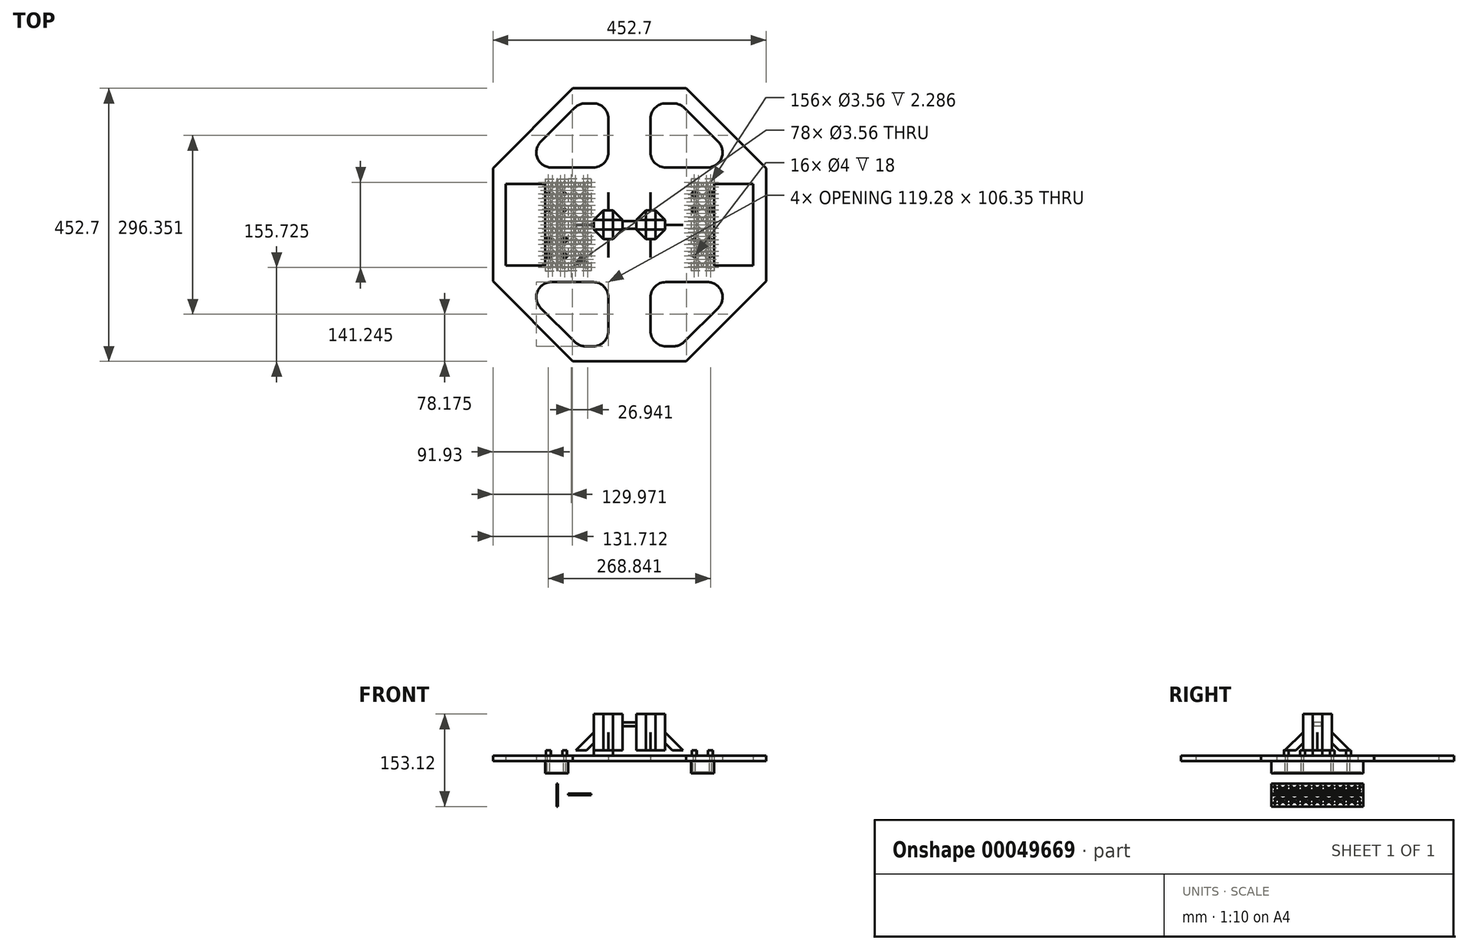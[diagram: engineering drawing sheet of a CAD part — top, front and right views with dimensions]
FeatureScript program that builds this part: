
annotation { "Feature Type Name" : "Feature", "Feature Type Description" : "" }
export const myFeature = defineFeature(function(context is Context, id is Id, definition is map)
    precondition{}
    {
        {
            var Q0;
            Q0=qCreatedBy(makeId("Top.planeOp"),FACE);
            var sketch = newSketch(context, id + "F0", { "sketchPlane" : qUnion([Q0])});
            skCircle(sketch, "E0.cCircle", {"center": v(0, 0) * mm, "radius": 245 * mm, "construction": true});
            skLineSegment(sketch, "E0.0", {"start": v(93.76, -226.35) * mm, "end": v(-93.76, -226.35) * mm});
            skLineSegment(sketch, "E0.1", {"start": v(-93.76, -226.35) * mm, "end": v(-226.35, -93.76) * mm});
            skLineSegment(sketch, "E0.2", {"start": v(-226.35, -93.76) * mm, "end": v(-226.35, 93.76) * mm});
            skLineSegment(sketch, "E0.3", {"start": v(-226.35, 93.76) * mm, "end": v(-93.76, 226.35) * mm});
            skLineSegment(sketch, "E0.4", {"start": v(-93.76, 226.35) * mm, "end": v(93.76, 226.35) * mm});
            skLineSegment(sketch, "E0.5", {"start": v(93.76, 226.35) * mm, "end": v(226.35, 93.76) * mm});
            skLineSegment(sketch, "E0.6", {"start": v(226.35, 93.76) * mm, "end": v(226.35, -93.76) * mm});
            skLineSegment(sketch, "E0.7", {"start": v(226.35, -93.76) * mm, "end": v(93.76, -226.35) * mm});
            skLineSegment(sketch, "E1", {"start": v(0, 226.35) * mm, "end": v(0, -226.35) * mm, "construction": true});
            skLineSegment(sketch, "E2.bottom", {"start": v(-205, 67.5) * mm, "end": v(-140, 67.5) * mm});
            skLineSegment(sketch, "E2.top", {"start": v(-205, -67.5) * mm, "end": v(-140, -67.5) * mm});
            skLineSegment(sketch, "E2.left", {"start": v(-205, 67.5) * mm, "end": v(-205, -67.5) * mm});
            skLineSegment(sketch, "E2.right", {"start": v(-140, 67.5) * mm, "end": v(-140, -67.5) * mm});
            skLineSegment(sketch, "E3.MirrorCS", {"start": v(205, 67.5) * mm, "end": v(205, -67.5) * mm});
            skLineSegment(sketch, "E4.MirrorCS", {"start": v(205, 67.5) * mm, "end": v(140, 67.5) * mm});
            skLineSegment(sketch, "E5.MirrorCS", {"start": v(205, -67.5) * mm, "end": v(140, -67.5) * mm});
            skLineSegment(sketch, "E6.MirrorCS", {"start": v(140, 67.5) * mm, "end": v(140, -67.5) * mm});
            skLineSegment(sketch, "E7.0", {"start": v(-90.72, -194.03) * mm, "end": v(-147.07, -137.68) * mm});
            skLineSegment(sketch, "E8.0", {"start": v(-226.35, -95) * mm, "end": v(-225.1, -95) * mm});
            skLineSegment(sketch, "E9.trimOffspring", {"start": v(-129.4, -95) * mm, "end": v(-60, -95) * mm});
            skLineSegment(sketch, "E10.trimOffspring", {"start": v(-60, -201.35) * mm, "end": v(-73.05, -201.35) * mm});
            skLineSegment(sketch, "E11.trimOffspring", {"start": v(-35, -120) * mm, "end": v(-35, -176.35) * mm});
            skPoint(sketch, "E12.visualSharp", {"position": v(-189.75, -95) * mm});
            skArc(sketch, "E12.filletArc", {"start": v(-129.4, -95) * mm, "mid": v(-152.5, -110.43) * mm, "end": v(-147.07, -137.68) * mm});
            skPoint(sketch, "E13.visualSharp", {"position": v(-35, -95) * mm});
            skArc(sketch, "E13.filletArc", {"start": v(-35, -120) * mm, "mid": v(-42.32, -102.32) * mm, "end": v(-60, -95) * mm});
            skPoint(sketch, "E14.visualSharp", {"position": v(-35, -201.35) * mm});
            skArc(sketch, "E14.filletArc", {"start": v(-60, -201.35) * mm, "mid": v(-42.32, -194.03) * mm, "end": v(-35, -176.35) * mm});
            skPoint(sketch, "E15.visualSharp", {"position": v(-83.4, -201.35) * mm});
            skArc(sketch, "E15.filletArc", {"start": v(-90.72, -194.03) * mm, "mid": v(-82.61, -199.45) * mm, "end": v(-73.05, -201.35) * mm});
            skArc(sketch, "E16.MirrorCS", {"start": v(90.72, -194.03) * mm, "mid": v(82.61, -199.45) * mm, "end": v(73.05, -201.35) * mm});
            skLineSegment(sketch, "E17.MirrorCS", {"start": v(60, -201.35) * mm, "end": v(73.05, -201.35) * mm});
            skArc(sketch, "E18.MirrorCS", {"start": v(35, -120) * mm, "mid": v(42.32, -102.32) * mm, "end": v(60, -95) * mm});
            skArc(sketch, "E19.MirrorCS", {"start": v(60, -201.35) * mm, "mid": v(42.32, -194.03) * mm, "end": v(35, -176.35) * mm});
            skPoint(sketch, "E20.MirrorP", {"position": v(83.4, -201.35) * mm});
            skPoint(sketch, "E21.MirrorP", {"position": v(35, -95) * mm});
            skPoint(sketch, "E22.MirrorP", {"position": v(35, -201.35) * mm});
            skLineSegment(sketch, "E23.MirrorCS", {"start": v(90.72, -194.03) * mm, "end": v(147.07, -137.68) * mm});
            skLineSegment(sketch, "E24.MirrorCS", {"start": v(129.4, -95) * mm, "end": v(60, -95) * mm});
            skLineSegment(sketch, "E25.MirrorCS", {"start": v(35, -120) * mm, "end": v(35, -176.35) * mm});
            skArc(sketch, "E26.MirrorCS", {"start": v(129.4, -95) * mm, "mid": v(152.5, -110.43) * mm, "end": v(147.07, -137.68) * mm});
            skLineSegment(sketch, "E27.MirrorCS", {"start": v(-60, 201.35) * mm, "end": v(-73.05, 201.35) * mm});
            skLineSegment(sketch, "E28.MirrorCS", {"start": v(60, 201.35) * mm, "end": v(73.05, 201.35) * mm});
            skArc(sketch, "E29.MirrorCS", {"start": v(90.72, 194.03) * mm, "mid": v(82.61, 199.45) * mm, "end": v(73.05, 201.35) * mm});
            skArc(sketch, "E30.MirrorCS", {"start": v(-90.72, 194.03) * mm, "mid": v(-82.61, 199.45) * mm, "end": v(-73.05, 201.35) * mm});
            skArc(sketch, "E31.MirrorCS", {"start": v(-35, 120) * mm, "mid": v(-42.32, 102.32) * mm, "end": v(-60, 95) * mm});
            skPoint(sketch, "E32.MirrorP", {"position": v(35, 95) * mm});
            skLineSegment(sketch, "E33.MirrorCS", {"start": v(-35, 120) * mm, "end": v(-35, 176.35) * mm});
            skPoint(sketch, "E34.MirrorP", {"position": v(-35, 95) * mm});
            skPoint(sketch, "E35.MirrorP", {"position": v(-83.4, 201.35) * mm});
            skArc(sketch, "E36.MirrorCS", {"start": v(129.4, 95) * mm, "mid": v(152.5, 110.43) * mm, "end": v(147.07, 137.68) * mm});
            skLineSegment(sketch, "E37.MirrorCS", {"start": v(35, 120) * mm, "end": v(35, 176.35) * mm});
            skPoint(sketch, "E38.MirrorP", {"position": v(83.4, 201.35) * mm});
            skArc(sketch, "E39.MirrorCS", {"start": v(35, 120) * mm, "mid": v(42.32, 102.32) * mm, "end": v(60, 95) * mm});
            skLineSegment(sketch, "E40.MirrorCS", {"start": v(-129.4, 95) * mm, "end": v(-60, 95) * mm});
            skPoint(sketch, "E41.MirrorP", {"position": v(-35, 201.35) * mm});
            skArc(sketch, "E42.MirrorCS", {"start": v(60, 201.35) * mm, "mid": v(42.32, 194.03) * mm, "end": v(35, 176.35) * mm});
            skPoint(sketch, "E43.MirrorP", {"position": v(35, 201.35) * mm});
            skLineSegment(sketch, "E44.MirrorCS", {"start": v(-90.72, 194.03) * mm, "end": v(-147.07, 137.68) * mm});
            skArc(sketch, "E45.MirrorCS", {"start": v(-60, 201.35) * mm, "mid": v(-42.32, 194.03) * mm, "end": v(-35, 176.35) * mm});
            skArc(sketch, "E46.MirrorCS", {"start": v(-129.4, 95) * mm, "mid": v(-152.5, 110.43) * mm, "end": v(-147.07, 137.68) * mm});
            skLineSegment(sketch, "E47.MirrorCS", {"start": v(129.4, 95) * mm, "end": v(60, 95) * mm});
            skLineSegment(sketch, "E48.MirrorCS", {"start": v(90.72, 194.03) * mm, "end": v(147.07, 137.68) * mm});
            skLineSegment(sketch, "E49.bottom", {"start": v(-140, 76.2) * mm, "end": v(-101.9, 76.2) * mm});
            skLineSegment(sketch, "E49.top", {"start": v(-140, -76.2) * mm, "end": v(-101.9, -76.2) * mm});
            skLineSegment(sketch, "E49.left", {"start": v(-140, 76.2) * mm, "end": v(-140, -76.2) * mm});
            skLineSegment(sketch, "E49.right", {"start": v(-101.9, 76.2) * mm, "end": v(-101.9, -76.2) * mm});
            skLineSegment(sketch, "E50.MirrorCS", {"start": v(101.9, 76.2) * mm, "end": v(101.9, -76.2) * mm});
            skLineSegment(sketch, "E51.MirrorCS", {"start": v(140, 76.2) * mm, "end": v(101.9, 76.2) * mm});
            skLineSegment(sketch, "E52.MirrorCS", {"start": v(140, 76.2) * mm, "end": v(140, -76.2) * mm});
            skLineSegment(sketch, "E53.MirrorCS", {"start": v(140, -76.2) * mm, "end": v(101.9, -76.2) * mm});
            skCircle(sketch, "E54", {"center": v(-134.41, 51.56) * mm, "radius": 2 * mm});
            skCircle(sketch, "E55.0.1.0", {"center": v(-134.41, 24.61) * mm, "radius": 2 * mm});
            skCircle(sketch, "E55.1.0.0", {"center": v(-107.46, 51.56) * mm, "radius": 2 * mm});
            skCircle(sketch, "E55.1.1.0", {"center": v(-107.46, 24.61) * mm, "radius": 2 * mm});
            skLineSegment(sketch, "E55.direction1", {"start": v(-134.41, 51.56) * mm, "end": v(-107.46, 51.56) * mm, "construction": true});
            skLineSegment(sketch, "E55.direction2", {"start": v(-134.41, 51.56) * mm, "end": v(-134.41, 24.61) * mm, "construction": true});
            skLineSegment(sketch, "E56", {"start": v(-140, 0) * mm, "end": v(-101.9, 0) * mm, "construction": true});
            skCircle(sketch, "E57.MirrorC", {"center": v(-107.46, -24.61) * mm, "radius": 2 * mm});
            skCircle(sketch, "E58.MirrorC", {"center": v(-134.41, -24.61) * mm, "radius": 2 * mm});
            skCircle(sketch, "E59.MirrorC", {"center": v(-107.46, -51.56) * mm, "radius": 2 * mm});
            skCircle(sketch, "E60.MirrorC", {"center": v(-134.41, -51.56) * mm, "radius": 2 * mm});
            skCircle(sketch, "E61.MirrorC", {"center": v(134.41, 51.56) * mm, "radius": 2 * mm});
            skCircle(sketch, "E62.MirrorC", {"center": v(107.46, 51.56) * mm, "radius": 2 * mm});
            skCircle(sketch, "E63.MirrorC", {"center": v(107.46, 24.61) * mm, "radius": 2 * mm});
            skCircle(sketch, "E64.MirrorC", {"center": v(134.41, 24.61) * mm, "radius": 2 * mm});
            skCircle(sketch, "E65.MirrorC", {"center": v(107.46, -24.61) * mm, "radius": 2 * mm});
            skCircle(sketch, "E66.MirrorC", {"center": v(107.46, -51.56) * mm, "radius": 2 * mm});
            skCircle(sketch, "E67.MirrorC", {"center": v(134.41, -51.56) * mm, "radius": 2 * mm});
            skCircle(sketch, "E68.MirrorC", {"center": v(134.41, -24.61) * mm, "radius": 2 * mm});
            skSolve(sketch);
        }
        {
            var Q0;
            Q0 = qSketchRegion(id + "F0", true);
            var Q1;
            {var subQ3=sQuery(id+"F0.wireOp",EDGE,"E49.bottom");Q1=makeQuery(id+"F0.imprint","IMPRINT",FACE,{"disambiguationData":[TD([[makeQuery(id+"F0.imprint","IMPRINT",EDGE,{"derivedFrom":subQ3}),-1.0]])]});}
            var Q2;
            Q2=makeQuery(id+"F0.imprint","IMPRINT",FACE,{"disambiguationData":[TD([[makeQuery(id+"F0.imprint","IMPRINT",EDGE,{"derivedFrom":sQuery(id+"F0.wireOp",EDGE,"E50.MirrorCS")}),1.0]])]});
            extrude(context, id + "F1", {"entities" : qUnion([Q0, Q1, Q2]), "depth" : 18 * mm});
        }
        {
            var Q0;
            Q0=makeQuery(id+"F1.opExtrude","CAP_FACE",FACE,{"disambiguationData":[OSD([sQuery(id+"F0.wireOp",EDGE,"E0.0"),sQuery(id+"F0.wireOp",EDGE,"E0.1"),sQuery(id+"F0.wireOp",EDGE,"E0.2"),sQuery(id+"F0.wireOp",EDGE,"E0.3"),sQuery(id+"F0.wireOp",EDGE,"E0.4"),sQuery(id+"F0.wireOp",EDGE,"E0.5"),sQuery(id+"F0.wireOp",EDGE,"E0.6"),sQuery(id+"F0.wireOp",EDGE,"E0.7"),sQuery(id+"F0.wireOp",EDGE,"E2.bottom"),sQuery(id+"F0.wireOp",EDGE,"E2.top"),sQuery(id+"F0.wireOp",EDGE,"E2.left"),sQuery(id+"F0.wireOp",EDGE,"E3.MirrorCS"),sQuery(id+"F0.wireOp",EDGE,"E4.MirrorCS"),sQuery(id+"F0.wireOp",EDGE,"E5.MirrorCS"),sQuery(id+"F0.wireOp",EDGE,"E7.0"),sQuery(id+"F0.wireOp",EDGE,"E9.trimOffspring"),sQuery(id+"F0.wireOp",EDGE,"E10.trimOffspring"),sQuery(id+"F0.wireOp",EDGE,"E11.trimOffspring"),sQuery(id+"F0.wireOp",EDGE,"E12.filletArc"),sQuery(id+"F0.wireOp",EDGE,"E13.filletArc"),sQuery(id+"F0.wireOp",EDGE,"E14.filletArc"),sQuery(id+"F0.wireOp",EDGE,"E15.filletArc"),sQuery(id+"F0.wireOp",EDGE,"E16.MirrorCS"),sQuery(id+"F0.wireOp",EDGE,"E17.MirrorCS"),sQuery(id+"F0.wireOp",EDGE,"E18.MirrorCS"),sQuery(id+"F0.wireOp",EDGE,"E19.MirrorCS"),sQuery(id+"F0.wireOp",EDGE,"E23.MirrorCS"),sQuery(id+"F0.wireOp",EDGE,"E24.MirrorCS"),sQuery(id+"F0.wireOp",EDGE,"E25.MirrorCS"),sQuery(id+"F0.wireOp",EDGE,"E26.MirrorCS"),sQuery(id+"F0.wireOp",EDGE,"E27.MirrorCS"),sQuery(id+"F0.wireOp",EDGE,"E28.MirrorCS"),sQuery(id+"F0.wireOp",EDGE,"E29.MirrorCS"),sQuery(id+"F0.wireOp",EDGE,"E30.MirrorCS"),sQuery(id+"F0.wireOp",EDGE,"E31.MirrorCS"),sQuery(id+"F0.wireOp",EDGE,"E33.MirrorCS"),sQuery(id+"F0.wireOp",EDGE,"E36.MirrorCS"),sQuery(id+"F0.wireOp",EDGE,"E37.MirrorCS"),sQuery(id+"F0.wireOp",EDGE,"E39.MirrorCS"),sQuery(id+"F0.wireOp",EDGE,"E40.MirrorCS"),sQuery(id+"F0.wireOp",EDGE,"E42.MirrorCS"),sQuery(id+"F0.wireOp",EDGE,"E44.MirrorCS"),sQuery(id+"F0.wireOp",EDGE,"E45.MirrorCS"),sQuery(id+"F0.wireOp",EDGE,"E46.MirrorCS"),sQuery(id+"F0.wireOp",EDGE,"E47.MirrorCS"),sQuery(id+"F0.wireOp",EDGE,"E48.MirrorCS"),sQuery(id+"F0.wireOp",EDGE,"E49.left"),sQuery(id+"F0.wireOp",EDGE,"E52.MirrorCS")])],"isStart":false});
            var sketch = newSketch(context, id + "F2", { "sketchPlane" : qUnion([Q0])});
            skPoint(sketch, "E69", {"position": v(0, 0) * mm});
            skPoint(sketch, "E70", {"position": v(-35, 0) * mm});
            skLineSegment(sketch, "E71.rect.bottom", {"start": v(-27.06, -7.94) * mm, "end": v(-42.94, -7.94) * mm});
            skLineSegment(sketch, "E71.rect.top", {"start": v(-27.06, 7.94) * mm, "end": v(-42.94, 7.94) * mm});
            skLineSegment(sketch, "E71.rect.left", {"start": v(-27.06, -7.94) * mm, "end": v(-27.06, 7.94) * mm});
            skLineSegment(sketch, "E71.rect.right", {"start": v(-42.94, -7.94) * mm, "end": v(-42.94, 7.94) * mm});
            skLineSegment(sketch, "E72.bottom", {"start": v(-42.94, 7.94) * mm, "end": v(-58.81, 7.94) * mm});
            skLineSegment(sketch, "E72.top", {"start": v(-42.94, -7.94) * mm, "end": v(-58.81, -7.94) * mm});
            skLineSegment(sketch, "E72.left", {"start": v(-42.94, 7.94) * mm, "end": v(-42.94, -7.94) * mm});
            skLineSegment(sketch, "E72.right", {"start": v(-58.81, 7.94) * mm, "end": v(-58.81, -7.94) * mm});
            skLineSegment(sketch, "E73", {"start": v(0, 0) * mm, "end": v(-35, 0) * mm, "construction": true});
            skLineSegment(sketch, "E74", {"start": v(-35, 0) * mm, "end": v(-58.81, 0) * mm, "construction": true});
            skCircle(sketch, "E75", {"center": v(-134.41, 51.56) * mm, "radius": 4 * mm});
            skCircle(sketch, "E76.0.1.0", {"center": v(-134.41, 24.61) * mm, "radius": 4 * mm});
            skCircle(sketch, "E76.1.0.0", {"center": v(-107.46, 51.56) * mm, "radius": 4 * mm});
            skCircle(sketch, "E76.1.1.0", {"center": v(-107.46, 24.61) * mm, "radius": 4 * mm});
            skLineSegment(sketch, "E76.direction1", {"start": v(-134.41, 51.56) * mm, "end": v(-107.46, 51.56) * mm, "construction": true});
            skLineSegment(sketch, "E76.direction2", {"start": v(-134.41, 51.56) * mm, "end": v(-134.41, 24.61) * mm, "construction": true});
            skLineSegment(sketch, "E77", {"start": v(0, 0) * mm, "end": v(0, 46.73) * mm, "construction": true});
            skCircle(sketch, "E78.MirrorC", {"center": v(-107.46, -51.56) * mm, "radius": 4 * mm});
            skCircle(sketch, "E79.MirrorC", {"center": v(-134.41, -51.56) * mm, "radius": 4 * mm});
            skCircle(sketch, "E80.MirrorC", {"center": v(-134.41, -24.61) * mm, "radius": 4 * mm});
            skCircle(sketch, "E81.MirrorC", {"center": v(-107.46, -24.61) * mm, "radius": 4 * mm});
            skCircle(sketch, "E82.MirrorC", {"center": v(107.46, -24.61) * mm, "radius": 4 * mm});
            skCircle(sketch, "E83.MirrorC", {"center": v(107.46, -51.56) * mm, "radius": 4 * mm});
            skCircle(sketch, "E84.MirrorC", {"center": v(134.41, -51.56) * mm, "radius": 4 * mm});
            skCircle(sketch, "E85.MirrorC", {"center": v(134.41, -24.61) * mm, "radius": 4 * mm});
            skCircle(sketch, "E86.MirrorC", {"center": v(107.46, 24.61) * mm, "radius": 4 * mm});
            skCircle(sketch, "E87.MirrorC", {"center": v(134.41, 24.61) * mm, "radius": 4 * mm});
            skCircle(sketch, "E88.MirrorC", {"center": v(134.41, 51.56) * mm, "radius": 4 * mm});
            skCircle(sketch, "E89.MirrorC", {"center": v(107.46, 51.56) * mm, "radius": 4 * mm});
            skSolve(sketch);
        }
        {
            var Q0;
            Q0=makeQuery(id+"F2.imprint","IMPRINT",FACE,{"disambiguationData":[TD([[makeQuery(id+"F2.imprint","IMPRINT",EDGE,{"derivedFrom":sQuery(id+"F2.wireOp",EDGE,"E75")}),1.0]])]});
            var Q1;
            Q1=makeQuery(id+"F2.imprint","IMPRINT",FACE,{"disambiguationData":[TD([[makeQuery(id+"F2.imprint","IMPRINT",EDGE,{"derivedFrom":sQuery(id+"F2.wireOp",EDGE,"E76.1.0.0")}),1.0]])]});
            var Q2;
            Q2=makeQuery(id+"F2.imprint","IMPRINT",FACE,{"disambiguationData":[TD([[makeQuery(id+"F2.imprint","IMPRINT",EDGE,{"derivedFrom":sQuery(id+"F2.wireOp",EDGE,"E76.0.1.0")}),1.0]])]});
            var Q3;
            Q3=makeQuery(id+"F2.imprint","IMPRINT",FACE,{"disambiguationData":[TD([[makeQuery(id+"F2.imprint","IMPRINT",EDGE,{"derivedFrom":sQuery(id+"F2.wireOp",EDGE,"E76.1.1.0")}),1.0]])]});
            var Q4;
            Q4=makeQuery(id+"F2.imprint","IMPRINT",FACE,{"disambiguationData":[TD([[makeQuery(id+"F2.imprint","IMPRINT",EDGE,{"derivedFrom":sQuery(id+"F2.wireOp",EDGE,"E80.MirrorC")}),-1.0]])]});
            var Q5;
            Q5=makeQuery(id+"F2.imprint","IMPRINT",FACE,{"disambiguationData":[TD([[makeQuery(id+"F2.imprint","IMPRINT",EDGE,{"derivedFrom":sQuery(id+"F2.wireOp",EDGE,"E81.MirrorC")}),-1.0]])]});
            var Q6;
            Q6=makeQuery(id+"F2.imprint","IMPRINT",FACE,{"disambiguationData":[TD([[makeQuery(id+"F2.imprint","IMPRINT",EDGE,{"derivedFrom":sQuery(id+"F2.wireOp",EDGE,"E79.MirrorC")}),-1.0]])]});
            var Q7;
            Q7=makeQuery(id+"F2.imprint","IMPRINT",FACE,{"disambiguationData":[TD([[makeQuery(id+"F2.imprint","IMPRINT",EDGE,{"derivedFrom":sQuery(id+"F2.wireOp",EDGE,"E78.MirrorC")}),-1.0]])]});
            var Q8;
            Q8=makeQuery(id+"F2.imprint","IMPRINT",FACE,{"disambiguationData":[TD([[makeQuery(id+"F2.imprint","IMPRINT",EDGE,{"derivedFrom":sQuery(id+"F2.wireOp",EDGE,"E89.MirrorC")}),-1.0]])]});
            var Q9;
            Q9=makeQuery(id+"F2.imprint","IMPRINT",FACE,{"disambiguationData":[TD([[makeQuery(id+"F2.imprint","IMPRINT",EDGE,{"derivedFrom":sQuery(id+"F2.wireOp",EDGE,"E88.MirrorC")}),-1.0]])]});
            var Q10;
            Q10=makeQuery(id+"F2.imprint","IMPRINT",FACE,{"disambiguationData":[TD([[makeQuery(id+"F2.imprint","IMPRINT",EDGE,{"derivedFrom":sQuery(id+"F2.wireOp",EDGE,"E86.MirrorC")}),-1.0]])]});
            var Q11;
            Q11=makeQuery(id+"F2.imprint","IMPRINT",FACE,{"disambiguationData":[TD([[makeQuery(id+"F2.imprint","IMPRINT",EDGE,{"derivedFrom":sQuery(id+"F2.wireOp",EDGE,"E87.MirrorC")}),-1.0]])]});
            var Q12;
            Q12=makeQuery(id+"F2.imprint","IMPRINT",FACE,{"disambiguationData":[TD([[makeQuery(id+"F2.imprint","IMPRINT",EDGE,{"derivedFrom":sQuery(id+"F2.wireOp",EDGE,"E82.MirrorC")}),1.0]])]});
            var Q13;
            Q13=makeQuery(id+"F2.imprint","IMPRINT",FACE,{"disambiguationData":[TD([[makeQuery(id+"F2.imprint","IMPRINT",EDGE,{"derivedFrom":sQuery(id+"F2.wireOp",EDGE,"E85.MirrorC")}),1.0]])]});
            var Q14;
            Q14=makeQuery(id+"F2.imprint","IMPRINT",FACE,{"disambiguationData":[TD([[makeQuery(id+"F2.imprint","IMPRINT",EDGE,{"derivedFrom":sQuery(id+"F2.wireOp",EDGE,"E83.MirrorC")}),1.0]])]});
            var Q15;
            Q15=makeQuery(id+"F2.imprint","IMPRINT",FACE,{"disambiguationData":[TD([[makeQuery(id+"F2.imprint","IMPRINT",EDGE,{"derivedFrom":sQuery(id+"F2.wireOp",EDGE,"E84.MirrorC")}),1.0]])]});
            var Q16;
            Q16=sQuery(id+"F2.wireOp",EDGE,"E75");
            extrude(context, id + "F3", {"entities" : qUnion([Q0, Q1, Q2, Q3, Q4, Q5, Q6, Q7, Q8, Q9, Q10, Q11, Q12, Q13, Q14, Q15]), "operationType" : NewBodyOperationType.REMOVE, "surfaceEntities" : qUnion([Q16]), "oppositeDirection" : true, "depth" : 9 * mm});
        }
        {
            var Q0;
            Q0=makeQuery(id+"F2.imprint","IMPRINT",FACE,{"disambiguationData":[TD([[makeQuery(id+"F2.imprint","IMPRINT",EDGE,{"derivedFrom":sQuery(id+"F2.wireOp",EDGE,"E72.bottom")}),1.0]])]});
            extrude(context, id + "F4", {"entities" : qUnion([Q0]), "depth" : 60 * mm});
        }
        {
            var Q0;
            Q0=makeQuery(id+"F4.opExtrude","CAP_FACE",FACE,{"disambiguationData":[OSD([sQuery(id+"F2.wireOp",EDGE,"E72.bottom"),sQuery(id+"F2.wireOp",EDGE,"E72.top"),sQuery(id+"F2.wireOp",EDGE,"E72.left"),sQuery(id+"F2.wireOp",EDGE,"E72.right")])],"isStart":false});
            var sketch = newSketch(context, id + "F5", { "sketchPlane" : qUnion([Q0])});
            skLineSegment(sketch, "E90", {"start": v(-42.94, -7.94) * mm, "end": v(-42.94, -23.81) * mm});
            skLineSegment(sketch, "E91", {"start": v(-42.94, -23.81) * mm, "end": v(-58.81, -7.94) * mm});
            skLineSegment(sketch, "E92", {"start": v(-58.81, 0) * mm, "end": v(-42.94, 0) * mm, "construction": true});
            skSolve(sketch);
        }
        {
            var Q0;
            Q0=makeQuery(id+"F5.imprint","IMPRINT",FACE,{"disambiguationData":[TD([[makeQuery(id+"F5.imprint","IMPRINT",EDGE,{"derivedFrom":sQuery(id+"F5.wireOp",EDGE,"E90")}),-1.0]])]});
            extrude(context, id + "F6", {"entities" : qUnion([Q0]), "oppositeDirection" : true, "depth" : 1 / 101.6 * mm});
        }
        {
            var Q0;
            Q0=qCreatedBy(makeId("Front.planeOp"),FACE);
            var sketch = newSketch(context, id + "F7", { "sketchPlane" : qUnion([Q0])});
            skLineSegment(sketch, "E93", {"start": v(0, 0) * mm, "end": v(-35, 0) * mm, "construction": true});
            skLineSegment(sketch, "E94", {"start": v(-35, 0) * mm, "end": v(-35, 90.39) * mm, "construction": true});
            skLineSegment(sketch, "E95.0.0", {"start": v(-58.81, 18) * mm, "end": v(-42.94, 18) * mm, "construction": true});
            skLineSegment(sketch, "E95.0.1", {"start": v(-42.94, 18) * mm, "end": v(-42.94, 78) * mm, "construction": true});
            skLineSegment(sketch, "E95.0.2", {"start": v(-42.94, 78) * mm, "end": v(-58.81, 78) * mm, "construction": true});
            skLineSegment(sketch, "E95.0.3", {"start": v(-58.81, 78) * mm, "end": v(-58.81, 18) * mm, "construction": true});
            skLineSegment(sketch, "E96", {"start": v(-58.81, 30.04) * mm, "end": v(-58.81, 48) * mm});
            skLineSegment(sketch, "E97", {"start": v(-70.85, 18) * mm, "end": v(-88.81, 18) * mm});
            skLineSegment(sketch, "E98", {"start": v(-88.81, 18) * mm, "end": v(-58.81, 48) * mm});
            skLineSegment(sketch, "E99.0", {"start": v(-70.85, 18) * mm, "end": v(-58.81, 30.04) * mm});
            skSolve(sketch);
        }
        {
            var Q0;
            Q0=makeQuery(id+"F7.imprint","IMPRINT",FACE,{"disambiguationData":[TD([[makeQuery(id+"F7.imprint","IMPRINT",EDGE,{"derivedFrom":sQuery(id+"F7.wireOp",EDGE,"E96")}),1.0]])]});
            extrude(context, id + "F8", {"entities" : qUnion([Q0]), "depth" : 1 / 203.2 * mm, "hasSecondDirection" : true, "secondDirectionOppositeDirection" : true, "secondDirectionDepth" : 1 / 203.2 * mm});
        }
        {
            var Q0;
            Q0=makeQuery(id+"F4.opExtrude","SWEPT_BODY",BODY,{"disambiguationData":[OSD([sQuery(id+"F2.wireOp",EDGE,"E72.bottom"),sQuery(id+"F2.wireOp",EDGE,"E72.top"),sQuery(id+"F2.wireOp",EDGE,"E72.left"),sQuery(id+"F2.wireOp",EDGE,"E72.right")])]});
            var Q1;
            Q1=makeQuery(id+"F6.opExtrude","SWEPT_BODY",BODY,{"disambiguationData":[OSD([sQuery(id+"F2.wireOp",EDGE,"E72.top"),sQuery(id+"F5.wireOp",EDGE,"E90"),sQuery(id+"F5.wireOp",EDGE,"E91")])]});
            var Q2;
            Q2=sQuery(id+"F7.wireOp",EDGE,"E94");
            circularPattern(context, id + "F9", {"entities" : qUnion([Q0, Q1]), "axis" : qUnion([Q2]), "angle" : 90 * degree, "instanceCount" : 4});
        }
        {
            var Q0;
            Q0=makeQuery(id+"F8.opExtrude","SWEPT_BODY",BODY,{"disambiguationData":[OSD([sQuery(id+"F7.wireOp",EDGE,"E96"),sQuery(id+"F7.wireOp",EDGE,"E97"),sQuery(id+"F7.wireOp",EDGE,"E98"),sQuery(id+"F7.wireOp",EDGE,"E99.0")])]});
            var Q1;
            Q1=sQuery(id+"F7.wireOp",EDGE,"E94");
            circularPattern(context, id + "F10", {"entities" : qUnion([Q0]), "axis" : qUnion([Q1]), "angle" : 90 * degree, "instanceCount" : 2});
        }
        {
            var Q0;
            Q0=makeQuery(id+"F8.opExtrude","SWEPT_BODY",BODY,{"disambiguationData":[OSD([sQuery(id+"F7.wireOp",EDGE,"E96"),sQuery(id+"F7.wireOp",EDGE,"E97"),sQuery(id+"F7.wireOp",EDGE,"E98"),sQuery(id+"F7.wireOp",EDGE,"E99.0")])]});
            var Q1;
            Q1=sQuery(id+"F7.wireOp",EDGE,"E94");
            circularPattern(context, id + "F11", {"entities" : qUnion([Q0]), "axis" : qUnion([Q1]), "angle" : 270 * degree, "instanceCount" : 2});
        }
        {
            var Q0;
            Q0=makeQuery(id+"F9.opPattern","COPY",FACE,{"derivedFrom":makeQuery(id+"F4.opExtrude","SWEPT_FACE",FACE,{"disambiguationData":[OSD([sQuery(id+"F2.wireOp",EDGE,"E72.right")])]}),"instanceName":"2"});
            var sketch = newSketch(context, id + "F12", { "sketchPlane" : qUnion([Q0])});
            skLineSegment(sketch, "E100", {"start": v(0, 18) * mm, "end": v(0, 78) * mm, "construction": true});
            skLineSegment(sketch, "E101", {"start": v(-7.94, 18) * mm, "end": v(7.94, 18) * mm, "construction": true});
            skLineSegment(sketch, "E102.0", {"start": v(-7.94, 58) * mm, "end": v(7.94, 58) * mm, "construction": true});
            skLineSegment(sketch, "E103.0", {"start": v(-7.94, 61.17) * mm, "end": v(7.94, 61.17) * mm, "construction": true});
            skLineSegment(sketch, "E104.rect.bottom", {"start": v(6.35, 64.35) * mm, "end": v(-6.35, 64.35) * mm});
            skLineSegment(sketch, "E104.rect.top", {"start": v(6.35, 58) * mm, "end": v(-6.35, 58) * mm});
            skLineSegment(sketch, "E104.rect.left", {"start": v(6.35, 64.35) * mm, "end": v(6.35, 58) * mm});
            skLineSegment(sketch, "E104.rect.right", {"start": v(-6.35, 64.35) * mm, "end": v(-6.35, 58) * mm});
            skPoint(sketch, "E104.rect.middle", {"position": v(0, 61.17) * mm});
            skSolve(sketch);
        }
        {
            var Q0;
            {var subQ3=sQuery(id+"F0.wireOp",EDGE,"E49.bottom");Q0=makeQuery(id+"F0.imprint","IMPRINT",FACE,{"disambiguationData":[TD([[makeQuery(id+"F0.imprint","IMPRINT",EDGE,{"derivedFrom":subQ3}),-1.0]])]});}
            extrude(context, id + "F13", {"entities" : qUnion([Q0]), "oppositeDirection" : true, "depth" : 18 * mm});
        }
        {
            var Q0;
            Q0=makeQuery(id+"F13.opExtrude","CAP_FACE",FACE,{"disambiguationData":[OSD([sQuery(id+"F0.wireOp",EDGE,"E49.bottom"),sQuery(id+"F0.wireOp",EDGE,"E49.top"),sQuery(id+"F0.wireOp",EDGE,"E49.left"),sQuery(id+"F0.wireOp",EDGE,"E49.right")])],"isStart":false});
            var sketch = newSketch(context, id + "F14", { "sketchPlane" : qUnion([Q0])});
            skLineSegment(sketch, "E105.bottom", {"start": v(-140, 76.2) * mm, "end": v(-101.9, 76.2) * mm});
            skLineSegment(sketch, "E105.top", {"start": v(-140, -76.2) * mm, "end": v(-101.9, -76.2) * mm});
            skLineSegment(sketch, "E105.left", {"start": v(-140, 76.2) * mm, "end": v(-140, -76.2) * mm});
            skLineSegment(sketch, "E105.right", {"start": v(-101.9, 76.2) * mm, "end": v(-101.9, -76.2) * mm});
            skLineSegment(sketch, "E106", {"start": v(-140, 0) * mm, "end": v(-101.9, 0) * mm, "construction": true});
            skLineSegment(sketch, "E107", {"start": v(-120.95, 76.2) * mm, "end": v(-120.95, -76.2) * mm, "construction": true});
            skLineSegment(sketch, "E108.0", {"start": v(-140, -57.15) * mm, "end": v(-101.9, -57.15) * mm, "construction": true});
            skLineSegment(sketch, "E109", {"start": v(-120.95, -57.15) * mm, "end": v(-101.9, -76.2) * mm, "construction": true});
            skCircle(sketch, "E110", {"center": v(-120.95, -57.15) * mm, "radius": 9.78 * mm, "construction": true});
            skCircle(sketch, "E111", {"center": v(-120.95, -57.15) * mm, "radius": 19.05 * mm, "construction": true});
            skCircle(sketch, "E112", {"center": v(-107.48, -70.62) * mm, "radius": 1.78 * mm});
            skCircle(sketch, "E113", {"center": v(-114.04, -64.06) * mm, "radius": 1.78 * mm});
            skCircle(sketch, "E114", {"center": v(-120.95, -66.93) * mm, "radius": 2.03 * mm});
            skCircle(sketch, "E115", {"center": v(-111.17, -57.15) * mm, "radius": 1.78 * mm});
            skCircle(sketch, "E116", {"center": v(-120.95, -57.15) * mm, "radius": 6.35 * mm});
            skCircle(sketch, "E117", {"center": v(-114.04, -69.3) * mm, "radius": 1.78 * mm});
            skCircle(sketch, "E118", {"center": v(-107.48, -62.73) * mm, "radius": 1.78 * mm});
            skCircle(sketch, "E119.MirrorC", {"center": v(-130.73, -57.15) * mm, "radius": 1.78 * mm});
            skCircle(sketch, "E120.MirrorC", {"center": v(-134.42, -70.62) * mm, "radius": 1.78 * mm});
            skCircle(sketch, "E121.MirrorC", {"center": v(-127.86, -69.3) * mm, "radius": 1.78 * mm});
            skCircle(sketch, "E122.MirrorC", {"center": v(-127.86, -64.06) * mm, "radius": 1.78 * mm});
            skCircle(sketch, "E123.MirrorC", {"center": v(-134.42, -62.73) * mm, "radius": 1.78 * mm});
            skCircle(sketch, "E124.1.0.0", {"center": v(-120.95, -38.1) * mm, "radius": 6.35 * mm});
            skCircle(sketch, "E124.1.0.1", {"center": v(-130.73, -38.1) * mm, "radius": 1.78 * mm});
            skCircle(sketch, "E124.1.0.2", {"center": v(-134.42, -43.68) * mm, "radius": 1.78 * mm});
            skCircle(sketch, "E124.1.0.3", {"center": v(-127.86, -45.01) * mm, "radius": 1.78 * mm});
            skCircle(sketch, "E124.1.0.4", {"center": v(-134.42, -51.57) * mm, "radius": 1.78 * mm});
            skCircle(sketch, "E124.1.0.5", {"center": v(-127.86, -50.24) * mm, "radius": 1.78 * mm});
            skCircle(sketch, "E124.1.0.6", {"center": v(-120.95, -47.88) * mm, "radius": 2.03 * mm});
            skCircle(sketch, "E124.1.0.7", {"center": v(-114.04, -50.24) * mm, "radius": 1.78 * mm});
            skCircle(sketch, "E124.1.0.8", {"center": v(-107.48, -51.57) * mm, "radius": 1.78 * mm});
            skCircle(sketch, "E124.1.0.9", {"center": v(-111.17, -38.1) * mm, "radius": 1.78 * mm});
            skCircle(sketch, "E124.1.0.10", {"center": v(-114.04, -45.01) * mm, "radius": 1.78 * mm});
            skCircle(sketch, "E124.1.0.11", {"center": v(-107.48, -43.68) * mm, "radius": 1.78 * mm});
            skCircle(sketch, "E124.2.0.0", {"center": v(-120.95, -19.05) * mm, "radius": 6.35 * mm});
            skCircle(sketch, "E124.2.0.1", {"center": v(-130.73, -19.05) * mm, "radius": 1.78 * mm});
            skCircle(sketch, "E124.2.0.2", {"center": v(-134.42, -24.63) * mm, "radius": 1.78 * mm});
            skCircle(sketch, "E124.2.0.3", {"center": v(-127.86, -25.96) * mm, "radius": 1.78 * mm});
            skCircle(sketch, "E124.2.0.4", {"center": v(-134.42, -32.52) * mm, "radius": 1.78 * mm});
            skCircle(sketch, "E124.2.0.5", {"center": v(-127.86, -31.2) * mm, "radius": 1.78 * mm});
            skCircle(sketch, "E124.2.0.6", {"center": v(-120.95, -28.83) * mm, "radius": 2.03 * mm});
            skCircle(sketch, "E124.2.0.7", {"center": v(-114.04, -31.2) * mm, "radius": 1.78 * mm});
            skCircle(sketch, "E124.2.0.8", {"center": v(-107.48, -32.52) * mm, "radius": 1.78 * mm});
            skCircle(sketch, "E124.2.0.9", {"center": v(-111.17, -19.05) * mm, "radius": 1.78 * mm});
            skCircle(sketch, "E124.2.0.10", {"center": v(-114.04, -25.96) * mm, "radius": 1.78 * mm});
            skCircle(sketch, "E124.2.0.11", {"center": v(-107.48, -24.63) * mm, "radius": 1.78 * mm});
            skCircle(sketch, "E124.3.0.0", {"center": v(-120.95, 0) * mm, "radius": 6.35 * mm});
            skCircle(sketch, "E124.3.0.1", {"center": v(-130.73, 0) * mm, "radius": 1.78 * mm});
            skCircle(sketch, "E124.3.0.2", {"center": v(-134.42, -5.58) * mm, "radius": 1.78 * mm});
            skCircle(sketch, "E124.3.0.3", {"center": v(-127.86, -6.91) * mm, "radius": 1.78 * mm});
            skCircle(sketch, "E124.3.0.4", {"center": v(-134.42, -13.47) * mm, "radius": 1.78 * mm});
            skCircle(sketch, "E124.3.0.5", {"center": v(-127.86, -12.14) * mm, "radius": 1.78 * mm});
            skCircle(sketch, "E124.3.0.6", {"center": v(-120.95, -9.78) * mm, "radius": 2.03 * mm});
            skCircle(sketch, "E124.3.0.7", {"center": v(-114.04, -12.14) * mm, "radius": 1.78 * mm});
            skCircle(sketch, "E124.3.0.8", {"center": v(-107.48, -13.47) * mm, "radius": 1.78 * mm});
            skCircle(sketch, "E124.3.0.9", {"center": v(-111.17, 0) * mm, "radius": 1.78 * mm});
            skCircle(sketch, "E124.3.0.10", {"center": v(-114.04, -6.91) * mm, "radius": 1.78 * mm});
            skCircle(sketch, "E124.3.0.11", {"center": v(-107.48, -5.58) * mm, "radius": 1.78 * mm});
            skCircle(sketch, "E124.4.0.0", {"center": v(-120.95, 19.05) * mm, "radius": 6.35 * mm});
            skCircle(sketch, "E124.4.0.1", {"center": v(-130.73, 19.05) * mm, "radius": 1.78 * mm});
            skCircle(sketch, "E124.4.0.2", {"center": v(-134.42, 13.47) * mm, "radius": 1.78 * mm});
            skCircle(sketch, "E124.4.0.3", {"center": v(-127.86, 12.14) * mm, "radius": 1.78 * mm});
            skCircle(sketch, "E124.4.0.4", {"center": v(-134.42, 5.58) * mm, "radius": 1.78 * mm});
            skCircle(sketch, "E124.4.0.5", {"center": v(-127.86, 6.9) * mm, "radius": 1.78 * mm});
            skCircle(sketch, "E124.4.0.6", {"center": v(-120.95, 9.27) * mm, "radius": 2.03 * mm});
            skCircle(sketch, "E124.4.0.7", {"center": v(-114.04, 6.9) * mm, "radius": 1.78 * mm});
            skCircle(sketch, "E124.4.0.8", {"center": v(-107.48, 5.58) * mm, "radius": 1.78 * mm});
            skCircle(sketch, "E124.4.0.9", {"center": v(-111.17, 19.05) * mm, "radius": 1.78 * mm});
            skCircle(sketch, "E124.4.0.10", {"center": v(-114.04, 12.14) * mm, "radius": 1.78 * mm});
            skCircle(sketch, "E124.4.0.11", {"center": v(-107.48, 13.47) * mm, "radius": 1.78 * mm});
            skCircle(sketch, "E124.5.0.0", {"center": v(-120.95, 38.1) * mm, "radius": 6.35 * mm});
            skCircle(sketch, "E124.5.0.1", {"center": v(-130.73, 38.1) * mm, "radius": 1.78 * mm});
            skCircle(sketch, "E124.5.0.2", {"center": v(-134.42, 32.52) * mm, "radius": 1.78 * mm});
            skCircle(sketch, "E124.5.0.3", {"center": v(-127.86, 31.19) * mm, "radius": 1.78 * mm});
            skCircle(sketch, "E124.5.0.4", {"center": v(-134.42, 24.63) * mm, "radius": 1.78 * mm});
            skCircle(sketch, "E124.5.0.5", {"center": v(-127.86, 25.96) * mm, "radius": 1.78 * mm});
            skCircle(sketch, "E124.5.0.6", {"center": v(-120.95, 28.32) * mm, "radius": 2.03 * mm});
            skCircle(sketch, "E124.5.0.7", {"center": v(-114.04, 25.96) * mm, "radius": 1.78 * mm});
            skCircle(sketch, "E124.5.0.8", {"center": v(-107.48, 24.63) * mm, "radius": 1.78 * mm});
            skCircle(sketch, "E124.5.0.9", {"center": v(-111.17, 38.1) * mm, "radius": 1.78 * mm});
            skCircle(sketch, "E124.5.0.10", {"center": v(-114.04, 31.19) * mm, "radius": 1.78 * mm});
            skCircle(sketch, "E124.5.0.11", {"center": v(-107.48, 32.52) * mm, "radius": 1.78 * mm});
            skCircle(sketch, "E124.6.0.0", {"center": v(-120.95, 57.15) * mm, "radius": 6.35 * mm});
            skCircle(sketch, "E124.6.0.1", {"center": v(-130.73, 57.15) * mm, "radius": 1.78 * mm});
            skCircle(sketch, "E124.6.0.2", {"center": v(-134.42, 51.57) * mm, "radius": 1.78 * mm});
            skCircle(sketch, "E124.6.0.3", {"center": v(-127.86, 50.24) * mm, "radius": 1.78 * mm});
            skCircle(sketch, "E124.6.0.4", {"center": v(-134.42, 43.68) * mm, "radius": 1.78 * mm});
            skCircle(sketch, "E124.6.0.5", {"center": v(-127.86, 45) * mm, "radius": 1.78 * mm});
            skCircle(sketch, "E124.6.0.6", {"center": v(-120.95, 47.37) * mm, "radius": 2.03 * mm});
            skCircle(sketch, "E124.6.0.7", {"center": v(-114.04, 45) * mm, "radius": 1.78 * mm});
            skCircle(sketch, "E124.6.0.8", {"center": v(-107.48, 43.68) * mm, "radius": 1.78 * mm});
            skCircle(sketch, "E124.6.0.9", {"center": v(-111.17, 57.15) * mm, "radius": 1.78 * mm});
            skCircle(sketch, "E124.6.0.10", {"center": v(-114.04, 50.24) * mm, "radius": 1.78 * mm});
            skCircle(sketch, "E124.6.0.11", {"center": v(-107.48, 51.57) * mm, "radius": 1.78 * mm});
            skLineSegment(sketch, "E124.direction1", {"start": v(-120.95, -57.15) * mm, "end": v(-120.95, -38.1) * mm, "construction": true});
            skCircle(sketch, "E125.4.7.0", {"center": v(-134.42, 70.62) * mm, "radius": 1.78 * mm});
            skCircle(sketch, "E125.6.7.0", {"center": v(-127.86, 69.29) * mm, "radius": 1.78 * mm});
            skCircle(sketch, "E125.8.7.0", {"center": v(-134.42, 62.73) * mm, "radius": 1.78 * mm});
            skCircle(sketch, "E125.10.7.0", {"center": v(-127.86, 64.06) * mm, "radius": 1.78 * mm});
            skCircle(sketch, "E125.12.7.0", {"center": v(-120.95, 66.42) * mm, "radius": 2.03 * mm});
            skCircle(sketch, "E125.14.7.0", {"center": v(-114.04, 64.06) * mm, "radius": 1.78 * mm});
            skCircle(sketch, "E125.16.7.0", {"center": v(-107.48, 62.73) * mm, "radius": 1.78 * mm});
            skCircle(sketch, "E125.20.7.0", {"center": v(-114.04, 69.29) * mm, "radius": 1.78 * mm});
            skCircle(sketch, "E125.22.7.0", {"center": v(-107.48, 70.62) * mm, "radius": 1.78 * mm});
            skSolve(sketch);
        }
        {
            var Q0;
            Q0 = qSketchRegion(id + "F14", true);
            extrude(context, id + "F15", {"entities" : qUnion([Q0]), "depth" : 2.3 * mm});
        }
        {
            var Q0;
            Q0=makeQuery(id+"F13.opExtrude","SWEPT_FACE",FACE,{"disambiguationData":[OSD([sQuery(id+"F0.wireOp",EDGE,"E49.right")])]});
            cPlane(context, id + "F16", {"entities" : qUnion([Q0]), "cplaneType" : CPlaneType.OFFSET, "offset" : 1.5 / 50.8 * mm, "oppositeDirection" : true, "width" : 150 * mm, "height" : 150 * mm});
        }
        {
            var Q0;
            Q0=makeQuery(id+"F13.opExtrude","SWEPT_FACE",FACE,{"disambiguationData":[OSD([sQuery(id+"F0.wireOp",EDGE,"E49.right")])]});
            var sketch = newSketch(context, id + "F17", { "sketchPlane" : qUnion([Q0])});
            skLineSegment(sketch, "E126.0", {"start": v(76.2, -37.05) * mm, "end": v(-76.2, -37.05) * mm, "construction": true});
            skSolve(sketch);
        }
        {
            var Q0;
            Q0=qCreatedBy(id+"F16.planeOp",FACE);
            var sketch = newSketch(context, id + "F18", { "sketchPlane" : qUnion([Q0])});
            skLineSegment(sketch, "E127.0", {"start": v(76.2, -37.05) * mm, "end": v(-76.2, -37.05) * mm, "construction": true});
            skSolve(sketch);
        }
        {
            var Q0;
            Q0=makeQuery(id+"F15.opExtrude","SWEPT_BODY",BODY,{"disambiguationData":[OSD([sQuery(id+"F14.wireOp",EDGE,"E105.bottom"),sQuery(id+"F14.wireOp",EDGE,"E105.top"),sQuery(id+"F14.wireOp",EDGE,"E105.left"),sQuery(id+"F14.wireOp",EDGE,"E105.right"),sQuery(id+"F14.wireOp",EDGE,"E112"),sQuery(id+"F14.wireOp",EDGE,"E113"),sQuery(id+"F14.wireOp",EDGE,"E114"),sQuery(id+"F14.wireOp",EDGE,"E115"),sQuery(id+"F14.wireOp",EDGE,"E116"),sQuery(id+"F14.wireOp",EDGE,"E117"),sQuery(id+"F14.wireOp",EDGE,"E118"),sQuery(id+"F14.wireOp",EDGE,"E119.MirrorC"),sQuery(id+"F14.wireOp",EDGE,"E120.MirrorC"),sQuery(id+"F14.wireOp",EDGE,"E121.MirrorC"),sQuery(id+"F14.wireOp",EDGE,"E122.MirrorC"),sQuery(id+"F14.wireOp",EDGE,"E123.MirrorC"),sQuery(id+"F14.wireOp",EDGE,"E124.1.0.0"),sQuery(id+"F14.wireOp",EDGE,"E124.1.0.1"),sQuery(id+"F14.wireOp",EDGE,"E124.1.0.2"),sQuery(id+"F14.wireOp",EDGE,"E124.1.0.3"),sQuery(id+"F14.wireOp",EDGE,"E124.1.0.4"),sQuery(id+"F14.wireOp",EDGE,"E124.1.0.5"),sQuery(id+"F14.wireOp",EDGE,"E124.1.0.6"),sQuery(id+"F14.wireOp",EDGE,"E124.1.0.7"),sQuery(id+"F14.wireOp",EDGE,"E124.1.0.8"),sQuery(id+"F14.wireOp",EDGE,"E124.1.0.9"),sQuery(id+"F14.wireOp",EDGE,"E124.1.0.10"),sQuery(id+"F14.wireOp",EDGE,"E124.1.0.11"),sQuery(id+"F14.wireOp",EDGE,"E124.2.0.0"),sQuery(id+"F14.wireOp",EDGE,"E124.2.0.1"),sQuery(id+"F14.wireOp",EDGE,"E124.2.0.2"),sQuery(id+"F14.wireOp",EDGE,"E124.2.0.3"),sQuery(id+"F14.wireOp",EDGE,"E124.2.0.4"),sQuery(id+"F14.wireOp",EDGE,"E124.2.0.5"),sQuery(id+"F14.wireOp",EDGE,"E124.2.0.6"),sQuery(id+"F14.wireOp",EDGE,"E124.2.0.7"),sQuery(id+"F14.wireOp",EDGE,"E124.2.0.8"),sQuery(id+"F14.wireOp",EDGE,"E124.2.0.9"),sQuery(id+"F14.wireOp",EDGE,"E124.2.0.10"),sQuery(id+"F14.wireOp",EDGE,"E124.2.0.11"),sQuery(id+"F14.wireOp",EDGE,"E124.3.0.0"),sQuery(id+"F14.wireOp",EDGE,"E124.3.0.1"),sQuery(id+"F14.wireOp",EDGE,"E124.3.0.2"),sQuery(id+"F14.wireOp",EDGE,"E124.3.0.3"),sQuery(id+"F14.wireOp",EDGE,"E124.3.0.4"),sQuery(id+"F14.wireOp",EDGE,"E124.3.0.5"),sQuery(id+"F14.wireOp",EDGE,"E124.3.0.6"),sQuery(id+"F14.wireOp",EDGE,"E124.3.0.7"),sQuery(id+"F14.wireOp",EDGE,"E124.3.0.8"),sQuery(id+"F14.wireOp",EDGE,"E124.3.0.9"),sQuery(id+"F14.wireOp",EDGE,"E124.3.0.10"),sQuery(id+"F14.wireOp",EDGE,"E124.3.0.11"),sQuery(id+"F14.wireOp",EDGE,"E124.4.0.0"),sQuery(id+"F14.wireOp",EDGE,"E124.4.0.1"),sQuery(id+"F14.wireOp",EDGE,"E124.4.0.2"),sQuery(id+"F14.wireOp",EDGE,"E124.4.0.3"),sQuery(id+"F14.wireOp",EDGE,"E124.4.0.4"),sQuery(id+"F14.wireOp",EDGE,"E124.4.0.5"),sQuery(id+"F14.wireOp",EDGE,"E124.4.0.6"),sQuery(id+"F14.wireOp",EDGE,"E124.4.0.7"),sQuery(id+"F14.wireOp",EDGE,"E124.4.0.8"),sQuery(id+"F14.wireOp",EDGE,"E124.4.0.9"),sQuery(id+"F14.wireOp",EDGE,"E124.4.0.10"),sQuery(id+"F14.wireOp",EDGE,"E124.4.0.11"),sQuery(id+"F14.wireOp",EDGE,"E124.5.0.0"),sQuery(id+"F14.wireOp",EDGE,"E124.5.0.1"),sQuery(id+"F14.wireOp",EDGE,"E124.5.0.2"),sQuery(id+"F14.wireOp",EDGE,"E124.5.0.3"),sQuery(id+"F14.wireOp",EDGE,"E124.5.0.4"),sQuery(id+"F14.wireOp",EDGE,"E124.5.0.5"),sQuery(id+"F14.wireOp",EDGE,"E124.5.0.6"),sQuery(id+"F14.wireOp",EDGE,"E124.5.0.7"),sQuery(id+"F14.wireOp",EDGE,"E124.5.0.8"),sQuery(id+"F14.wireOp",EDGE,"E124.5.0.9"),sQuery(id+"F14.wireOp",EDGE,"E124.5.0.10"),sQuery(id+"F14.wireOp",EDGE,"E124.5.0.11"),sQuery(id+"F14.wireOp",EDGE,"E124.6.0.0"),sQuery(id+"F14.wireOp",EDGE,"E124.6.0.1"),sQuery(id+"F14.wireOp",EDGE,"E124.6.0.2"),sQuery(id+"F14.wireOp",EDGE,"E124.6.0.3"),sQuery(id+"F14.wireOp",EDGE,"E124.6.0.4"),sQuery(id+"F14.wireOp",EDGE,"E124.6.0.5"),sQuery(id+"F14.wireOp",EDGE,"E124.6.0.6"),sQuery(id+"F14.wireOp",EDGE,"E124.6.0.7"),sQuery(id+"F14.wireOp",EDGE,"E124.6.0.8"),sQuery(id+"F14.wireOp",EDGE,"E124.6.0.9"),sQuery(id+"F14.wireOp",EDGE,"E124.6.0.10"),sQuery(id+"F14.wireOp",EDGE,"E124.6.0.11"),sQuery(id+"F14.wireOp",EDGE,"E125.4.7.0"),sQuery(id+"F14.wireOp",EDGE,"E125.6.7.0"),sQuery(id+"F14.wireOp",EDGE,"E125.8.7.0"),sQuery(id+"F14.wireOp",EDGE,"E125.10.7.0"),sQuery(id+"F14.wireOp",EDGE,"E125.12.7.0"),sQuery(id+"F14.wireOp",EDGE,"E125.14.7.0"),sQuery(id+"F14.wireOp",EDGE,"E125.16.7.0"),sQuery(id+"F14.wireOp",EDGE,"E125.20.7.0"),sQuery(id+"F14.wireOp",EDGE,"E125.22.7.0")])]});
            var Q1;
            Q1=sQuery(id+"F18.wireOp",EDGE,"E127.0");
            circularPattern(context, id + "F19", {"operationType" : NewBodyOperationType.ADD, "entities" : qUnion([Q0]), "axis" : qUnion([Q1]), "angle" : 90 * degree, "instanceCount" : 3});
        }
        {
            var Q0;
            Q0=makeQuery(id+"F4.opExtrude","SWEPT_BODY",BODY,{"disambiguationData":[OSD([sQuery(id+"F2.wireOp",EDGE,"E72.bottom"),sQuery(id+"F2.wireOp",EDGE,"E72.top"),sQuery(id+"F2.wireOp",EDGE,"E72.left"),sQuery(id+"F2.wireOp",EDGE,"E72.right")])]});
            var Q1;
            Q1=makeQuery(id+"F6.opExtrude","SWEPT_BODY",BODY,{"disambiguationData":[OSD([sQuery(id+"F2.wireOp",EDGE,"E72.top"),sQuery(id+"F5.wireOp",EDGE,"E90"),sQuery(id+"F5.wireOp",EDGE,"E91")])]});
            var Q2;
            Q2=makeQuery(id+"F8.opExtrude","SWEPT_BODY",BODY,{"disambiguationData":[OSD([sQuery(id+"F7.wireOp",EDGE,"E96"),sQuery(id+"F7.wireOp",EDGE,"E97"),sQuery(id+"F7.wireOp",EDGE,"E98"),sQuery(id+"F7.wireOp",EDGE,"E99.0")])]});
            var Q3;
            Q3=makeQuery(id+"F9.opPattern","COPY",BODY,{"derivedFrom":makeQuery(id+"F4.opExtrude","SWEPT_BODY",BODY,{"disambiguationData":[OSD([sQuery(id+"F2.wireOp",EDGE,"E72.bottom"),sQuery(id+"F2.wireOp",EDGE,"E72.top"),sQuery(id+"F2.wireOp",EDGE,"E72.left"),sQuery(id+"F2.wireOp",EDGE,"E72.right")])]}),"instanceName":"1"});
            var Q4;
            Q4=makeQuery(id+"F9.opPattern","COPY",BODY,{"derivedFrom":makeQuery(id+"F6.opExtrude","SWEPT_BODY",BODY,{"disambiguationData":[OSD([sQuery(id+"F2.wireOp",EDGE,"E72.top"),sQuery(id+"F5.wireOp",EDGE,"E90"),sQuery(id+"F5.wireOp",EDGE,"E91")])]}),"instanceName":"1"});
            var Q5;
            Q5=makeQuery(id+"F9.opPattern","COPY",BODY,{"derivedFrom":makeQuery(id+"F4.opExtrude","SWEPT_BODY",BODY,{"disambiguationData":[OSD([sQuery(id+"F2.wireOp",EDGE,"E72.bottom"),sQuery(id+"F2.wireOp",EDGE,"E72.top"),sQuery(id+"F2.wireOp",EDGE,"E72.left"),sQuery(id+"F2.wireOp",EDGE,"E72.right")])]}),"instanceName":"2"});
            var Q6;
            Q6=makeQuery(id+"F9.opPattern","COPY",BODY,{"derivedFrom":makeQuery(id+"F6.opExtrude","SWEPT_BODY",BODY,{"disambiguationData":[OSD([sQuery(id+"F2.wireOp",EDGE,"E72.top"),sQuery(id+"F5.wireOp",EDGE,"E90"),sQuery(id+"F5.wireOp",EDGE,"E91")])]}),"instanceName":"2"});
            var Q7;
            Q7=makeQuery(id+"F9.opPattern","COPY",BODY,{"derivedFrom":makeQuery(id+"F4.opExtrude","SWEPT_BODY",BODY,{"disambiguationData":[OSD([sQuery(id+"F2.wireOp",EDGE,"E72.bottom"),sQuery(id+"F2.wireOp",EDGE,"E72.top"),sQuery(id+"F2.wireOp",EDGE,"E72.left"),sQuery(id+"F2.wireOp",EDGE,"E72.right")])]}),"instanceName":"3"});
            var Q8;
            Q8=makeQuery(id+"F9.opPattern","COPY",BODY,{"derivedFrom":makeQuery(id+"F6.opExtrude","SWEPT_BODY",BODY,{"disambiguationData":[OSD([sQuery(id+"F2.wireOp",EDGE,"E72.top"),sQuery(id+"F5.wireOp",EDGE,"E90"),sQuery(id+"F5.wireOp",EDGE,"E91")])]}),"instanceName":"3"});
            var Q9;
            Q9=makeQuery(id+"F10.opPattern","COPY",BODY,{"derivedFrom":makeQuery(id+"F8.opExtrude","SWEPT_BODY",BODY,{"disambiguationData":[OSD([sQuery(id+"F7.wireOp",EDGE,"E96"),sQuery(id+"F7.wireOp",EDGE,"E97"),sQuery(id+"F7.wireOp",EDGE,"E98"),sQuery(id+"F7.wireOp",EDGE,"E99.0")])]}),"instanceName":"1"});
            var Q10;
            Q10=makeQuery(id+"F11.opPattern","COPY",BODY,{"derivedFrom":makeQuery(id+"F8.opExtrude","SWEPT_BODY",BODY,{"disambiguationData":[OSD([sQuery(id+"F7.wireOp",EDGE,"E96"),sQuery(id+"F7.wireOp",EDGE,"E97"),sQuery(id+"F7.wireOp",EDGE,"E98"),sQuery(id+"F7.wireOp",EDGE,"E99.0")])]}),"instanceName":"1"});
            var Q11;
            Q11=makeQuery(id+"F13.opExtrude","SWEPT_BODY",BODY,{"disambiguationData":[OSD([sQuery(id+"F0.wireOp",EDGE,"E49.bottom"),sQuery(id+"F0.wireOp",EDGE,"E49.top"),sQuery(id+"F0.wireOp",EDGE,"E49.left"),sQuery(id+"F0.wireOp",EDGE,"E49.right")])]});
            var Q12;
            Q12=makeQuery(id+"F15.opExtrude","SWEPT_BODY",BODY,{"disambiguationData":[OSD([sQuery(id+"F14.wireOp",EDGE,"E105.bottom"),sQuery(id+"F14.wireOp",EDGE,"E105.top"),sQuery(id+"F14.wireOp",EDGE,"E105.left"),sQuery(id+"F14.wireOp",EDGE,"E105.right"),sQuery(id+"F14.wireOp",EDGE,"E112"),sQuery(id+"F14.wireOp",EDGE,"E113"),sQuery(id+"F14.wireOp",EDGE,"E114"),sQuery(id+"F14.wireOp",EDGE,"E115"),sQuery(id+"F14.wireOp",EDGE,"E116"),sQuery(id+"F14.wireOp",EDGE,"E117"),sQuery(id+"F14.wireOp",EDGE,"E118"),sQuery(id+"F14.wireOp",EDGE,"E119.MirrorC"),sQuery(id+"F14.wireOp",EDGE,"E120.MirrorC"),sQuery(id+"F14.wireOp",EDGE,"E121.MirrorC"),sQuery(id+"F14.wireOp",EDGE,"E122.MirrorC"),sQuery(id+"F14.wireOp",EDGE,"E123.MirrorC"),sQuery(id+"F14.wireOp",EDGE,"E124.1.0.0"),sQuery(id+"F14.wireOp",EDGE,"E124.1.0.1"),sQuery(id+"F14.wireOp",EDGE,"E124.1.0.2"),sQuery(id+"F14.wireOp",EDGE,"E124.1.0.3"),sQuery(id+"F14.wireOp",EDGE,"E124.1.0.4"),sQuery(id+"F14.wireOp",EDGE,"E124.1.0.5"),sQuery(id+"F14.wireOp",EDGE,"E124.1.0.6"),sQuery(id+"F14.wireOp",EDGE,"E124.1.0.7"),sQuery(id+"F14.wireOp",EDGE,"E124.1.0.8"),sQuery(id+"F14.wireOp",EDGE,"E124.1.0.9"),sQuery(id+"F14.wireOp",EDGE,"E124.1.0.10"),sQuery(id+"F14.wireOp",EDGE,"E124.1.0.11"),sQuery(id+"F14.wireOp",EDGE,"E124.2.0.0"),sQuery(id+"F14.wireOp",EDGE,"E124.2.0.1"),sQuery(id+"F14.wireOp",EDGE,"E124.2.0.2"),sQuery(id+"F14.wireOp",EDGE,"E124.2.0.3"),sQuery(id+"F14.wireOp",EDGE,"E124.2.0.4"),sQuery(id+"F14.wireOp",EDGE,"E124.2.0.5"),sQuery(id+"F14.wireOp",EDGE,"E124.2.0.6"),sQuery(id+"F14.wireOp",EDGE,"E124.2.0.7"),sQuery(id+"F14.wireOp",EDGE,"E124.2.0.8"),sQuery(id+"F14.wireOp",EDGE,"E124.2.0.9"),sQuery(id+"F14.wireOp",EDGE,"E124.2.0.10"),sQuery(id+"F14.wireOp",EDGE,"E124.2.0.11"),sQuery(id+"F14.wireOp",EDGE,"E124.3.0.0"),sQuery(id+"F14.wireOp",EDGE,"E124.3.0.1"),sQuery(id+"F14.wireOp",EDGE,"E124.3.0.2"),sQuery(id+"F14.wireOp",EDGE,"E124.3.0.3"),sQuery(id+"F14.wireOp",EDGE,"E124.3.0.4"),sQuery(id+"F14.wireOp",EDGE,"E124.3.0.5"),sQuery(id+"F14.wireOp",EDGE,"E124.3.0.6"),sQuery(id+"F14.wireOp",EDGE,"E124.3.0.7"),sQuery(id+"F14.wireOp",EDGE,"E124.3.0.8"),sQuery(id+"F14.wireOp",EDGE,"E124.3.0.9"),sQuery(id+"F14.wireOp",EDGE,"E124.3.0.10"),sQuery(id+"F14.wireOp",EDGE,"E124.3.0.11"),sQuery(id+"F14.wireOp",EDGE,"E124.4.0.0"),sQuery(id+"F14.wireOp",EDGE,"E124.4.0.1"),sQuery(id+"F14.wireOp",EDGE,"E124.4.0.2"),sQuery(id+"F14.wireOp",EDGE,"E124.4.0.3"),sQuery(id+"F14.wireOp",EDGE,"E124.4.0.4"),sQuery(id+"F14.wireOp",EDGE,"E124.4.0.5"),sQuery(id+"F14.wireOp",EDGE,"E124.4.0.6"),sQuery(id+"F14.wireOp",EDGE,"E124.4.0.7"),sQuery(id+"F14.wireOp",EDGE,"E124.4.0.8"),sQuery(id+"F14.wireOp",EDGE,"E124.4.0.9"),sQuery(id+"F14.wireOp",EDGE,"E124.4.0.10"),sQuery(id+"F14.wireOp",EDGE,"E124.4.0.11"),sQuery(id+"F14.wireOp",EDGE,"E124.5.0.0"),sQuery(id+"F14.wireOp",EDGE,"E124.5.0.1"),sQuery(id+"F14.wireOp",EDGE,"E124.5.0.2"),sQuery(id+"F14.wireOp",EDGE,"E124.5.0.3"),sQuery(id+"F14.wireOp",EDGE,"E124.5.0.4"),sQuery(id+"F14.wireOp",EDGE,"E124.5.0.5"),sQuery(id+"F14.wireOp",EDGE,"E124.5.0.6"),sQuery(id+"F14.wireOp",EDGE,"E124.5.0.7"),sQuery(id+"F14.wireOp",EDGE,"E124.5.0.8"),sQuery(id+"F14.wireOp",EDGE,"E124.5.0.9"),sQuery(id+"F14.wireOp",EDGE,"E124.5.0.10"),sQuery(id+"F14.wireOp",EDGE,"E124.5.0.11"),sQuery(id+"F14.wireOp",EDGE,"E124.6.0.0"),sQuery(id+"F14.wireOp",EDGE,"E124.6.0.1"),sQuery(id+"F14.wireOp",EDGE,"E124.6.0.2"),sQuery(id+"F14.wireOp",EDGE,"E124.6.0.3"),sQuery(id+"F14.wireOp",EDGE,"E124.6.0.4"),sQuery(id+"F14.wireOp",EDGE,"E124.6.0.5"),sQuery(id+"F14.wireOp",EDGE,"E124.6.0.6"),sQuery(id+"F14.wireOp",EDGE,"E124.6.0.7"),sQuery(id+"F14.wireOp",EDGE,"E124.6.0.8"),sQuery(id+"F14.wireOp",EDGE,"E124.6.0.9"),sQuery(id+"F14.wireOp",EDGE,"E124.6.0.10"),sQuery(id+"F14.wireOp",EDGE,"E124.6.0.11"),sQuery(id+"F14.wireOp",EDGE,"E125.4.7.0"),sQuery(id+"F14.wireOp",EDGE,"E125.6.7.0"),sQuery(id+"F14.wireOp",EDGE,"E125.8.7.0"),sQuery(id+"F14.wireOp",EDGE,"E125.10.7.0"),sQuery(id+"F14.wireOp",EDGE,"E125.12.7.0"),sQuery(id+"F14.wireOp",EDGE,"E125.14.7.0"),sQuery(id+"F14.wireOp",EDGE,"E125.16.7.0"),sQuery(id+"F14.wireOp",EDGE,"E125.20.7.0"),sQuery(id+"F14.wireOp",EDGE,"E125.22.7.0")])]});
            var Q13;
            Q13=qCreatedBy(makeId("Right.planeOp"),FACE);
            mirror(context, id + "F20", {"entities" : qUnion([Q0, Q1, Q2, Q3, Q4, Q5, Q6, Q7, Q8, Q9, Q10, Q11, Q12]), "mirrorPlane" : qUnion([Q13])});
        }
        {
            var Q0;
            Q0=makeQuery(id+"F12.imprint","IMPRINT",FACE,{"disambiguationData":[TD([[makeQuery(id+"F12.imprint","IMPRINT",EDGE,{"derivedFrom":sQuery(id+"F12.wireOp",EDGE,"E104.rect.bottom")}),1.0]])]});
            var Q1;
            Q1=makeQuery(id+"F20.opPattern","COPY",FACE,{"derivedFrom":makeQuery(id+"F9.opPattern","COPY",FACE,{"derivedFrom":makeQuery(id+"F4.opExtrude","SWEPT_FACE",FACE,{"disambiguationData":[OSD([sQuery(id+"F2.wireOp",EDGE,"E72.right")])]}),"instanceName":"2"}),"instanceName":"1"});
            extrude(context, id + "F21", {"entities" : qUnion([Q0]), "endBound" : BoundingType.UP_TO_SURFACE, "endBoundEntityFace" : qUnion([Q1]), "depth" : 25 * mm});
        }
    });
